# Revit family: Gira_046603
name_source: partatom
category: Elektroinstallationen
revit_build: Autodesk Revit 2017 (Build: 20160225_1515(x64)
units: mm (PartAtom-declared; Revit-internal decimal feet)

## family parameters
Basisbauteil = Fläche
Beim Laden mit Abzugskörper schneiden = Nein
Bemaßung runder Anschluss = Durchmesser verwenden
Beschriftungsausrichtung beibehalten = Ja
Gemeinsam genutzt = Nein
Raumberechnungspunkt = Nein
Teiletyp = Normal

## types (1)
- Gira_046603
    Abschließbar = Nein
    Anschlussart = Steckklemme
    Antibakterielle Behandlung = Nein
    Anzahl der Einheiten = 1
    Anzahl der Module (bei Modulbauweise) = 1
    Anzahl der Steckdosen schaltbar = 0
    Aufdruck/Kennzeichnung = ohne Aufdruck
    Ausführung = SCHUKO
    Ausführung der Oberfläche = glänzend
    Auswurfmechanismus = Nein
    BIM = https://media.stage.bim.site
    Befestigungsart = Befestigung mit Schraube
    Beschreibung = SCHUKO-Steckdose 16 A 250 V~ ohne Befestigungskrallen  Reinweiß glänzend
    Cremeweiß glänzend = Cremeweiß glänzend
    Datenblatt = https://katalog.gira.de
    Farbe = weiß
    Fehlerstromschutz = Nein
    Frequenz [Hz] = [50:50]
    Für "erschwerte Bedingungen" (nach VDE) = Nein
    GTIN = 4010337466031
    Geeignet für Schutzart (IP) = IP20
    HAN = 046603
    Halogenfrei = Ja
    Hersteller = Gira
    Isolierter Einbau = Nein
    Min. Tiefe der Gerätedose [m] = 0.032
    Mit Durchschleiffunktion = Nein
    Mit Ein-/Ausschalter = Nein
    Mit Feinsicherung = Nein
    Mit Funktionsbeleuchtung = Nein
    Mit Klappdeckel = Nein
    Mit Orientierungsbeleuchtung = Nein
    Mit Signallampe = Nein
    Mit eingebauter USB-Spannungsversorgung = Nein
    Mit erhöhtem Berührungsschutz = Nein
    Modell = SYS55_Steckdose
    Montageart = Unterputz
    Nennspannung [Volt] 12 = 250
    Nennspannung [Volt] 14 = 250
    Nennstrom = 16 A
    Oberfläche = sonstige
    Produktseite = http://katalog.gira.de
    RAL-Nummer (ähnlich) = 9010
    Schutzkontakt = Ja
    Schutzleiterkontakt rund = Nein
    Sonderstromversorgung = ohne Sonderstromversorgung
    Textfeld/Beschriftungsfläche = Nein
    Transparent = Nein
    Typname = SCHUKO o.Kr. System 55 Reinweiß
    URL = https://www.gira.de
    Verdrehter Zentraleinsatz = Nein
    Vorgabe-Ansicht = 1219 mm
    Werkstoff = Kunststoff
    Werkstoffgüte = Thermoplast
    Überspannungsschutz = Nein

## geometry (parser evidence)
native form markers: Sweep x2
no freeform markers — native parametric forms only
